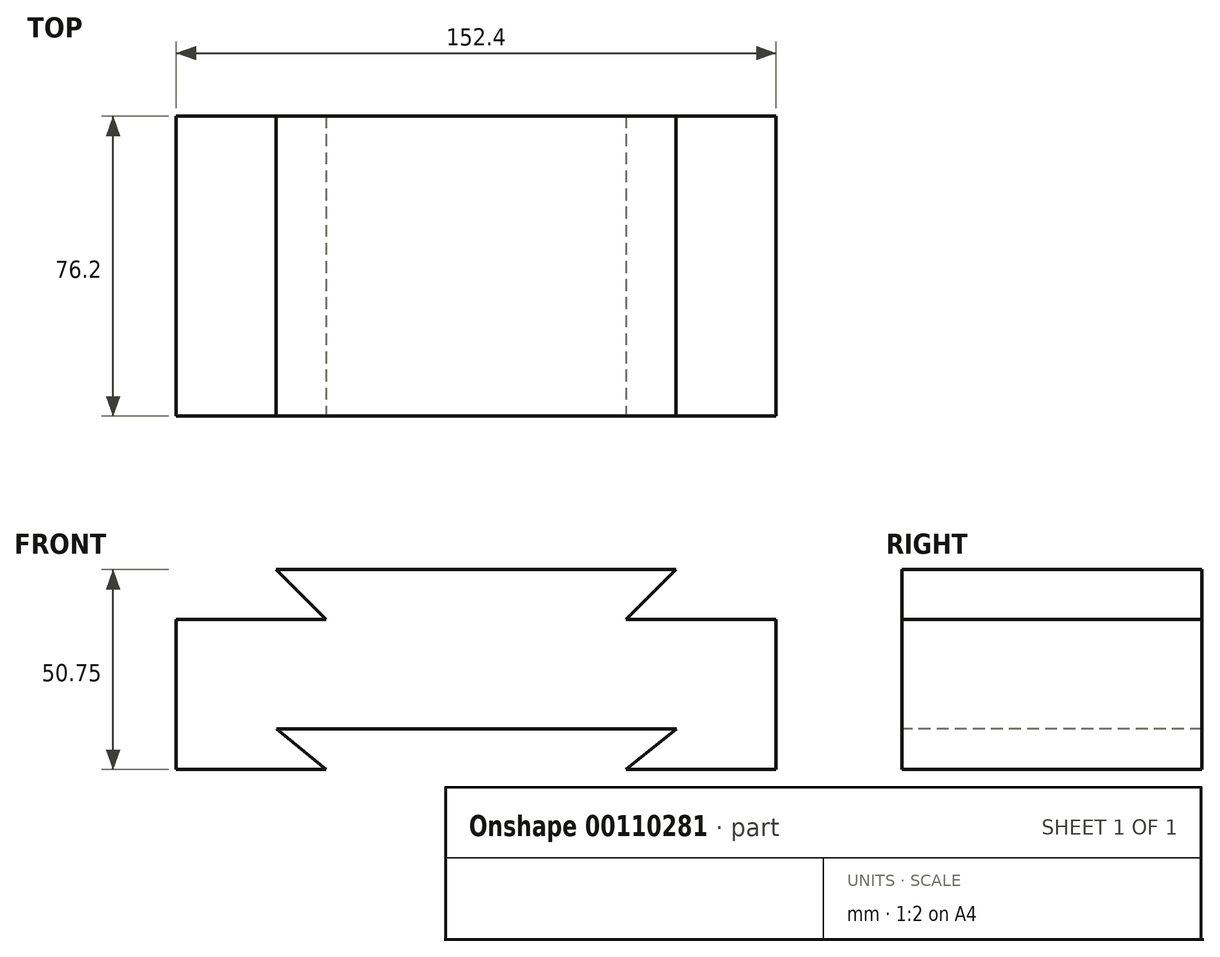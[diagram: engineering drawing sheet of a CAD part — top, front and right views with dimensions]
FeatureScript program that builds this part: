
annotation { "Feature Type Name" : "Feature", "Feature Type Description" : "" }
export const myFeature = defineFeature(function(context is Context, id is Id, definition is map)
    precondition{}
    {
        {
            var Q0;
            Q0=qCreatedBy(makeId("Front.planeOp"),FACE);
            var sketch = newSketch(context, id + "F0", { "sketchPlane" : qUnion([Q0])});
            skLineSegment(sketch, "E0", {"start": v(0, 0) * mm, "end": v(38.1, 0) * mm});
            skLineSegment(sketch, "E1", {"start": v(38.1, 0) * mm, "end": v(38.1, 38.1) * mm});
            skLineSegment(sketch, "E2", {"start": v(38.1, 38.1) * mm, "end": v(0, 38.1) * mm});
            skLineSegment(sketch, "E3", {"start": v(0, 38.1) * mm, "end": v(12.7, 50.75) * mm});
            skLineSegment(sketch, "E4", {"start": v(12.7, 50.75) * mm, "end": v(-88.9, 50.75) * mm});
            skLineSegment(sketch, "E5", {"start": v(-88.9, 50.75) * mm, "end": v(-76.2, 38.1) * mm});
            skLineSegment(sketch, "E6", {"start": v(-76.2, 38.1) * mm, "end": v(-114.3, 38.1) * mm});
            skLineSegment(sketch, "E7", {"start": v(-114.3, 38.1) * mm, "end": v(-114.3, 0) * mm});
            skLineSegment(sketch, "E8", {"start": v(-114.3, 0) * mm, "end": v(-76.2, 0) * mm});
            skLineSegment(sketch, "E9", {"start": v(-76.2, 0) * mm, "end": v(-88.85, 10.28) * mm});
            skLineSegment(sketch, "E10", {"start": v(-88.85, 10.28) * mm, "end": v(12.75, 10.28) * mm});
            skLineSegment(sketch, "E11", {"start": v(12.75, 10.28) * mm, "end": v(0, 0) * mm});
            skSolve(sketch);
        }
        {
            var Q0;
            Q0=makeQuery(id+"F0.imprint","IMPRINT",FACE,{"disambiguationData":[TD([[makeQuery(id+"F0.imprint","IMPRINT",EDGE,{"derivedFrom":sQuery(id+"F0.wireOp",EDGE,"E0")}),1.0]])]});
            extrude(context, id + "F1", {"entities" : qUnion([Q0]), "oppositeDirection" : true, "depth" : 76.2 * mm});
        }
    });
